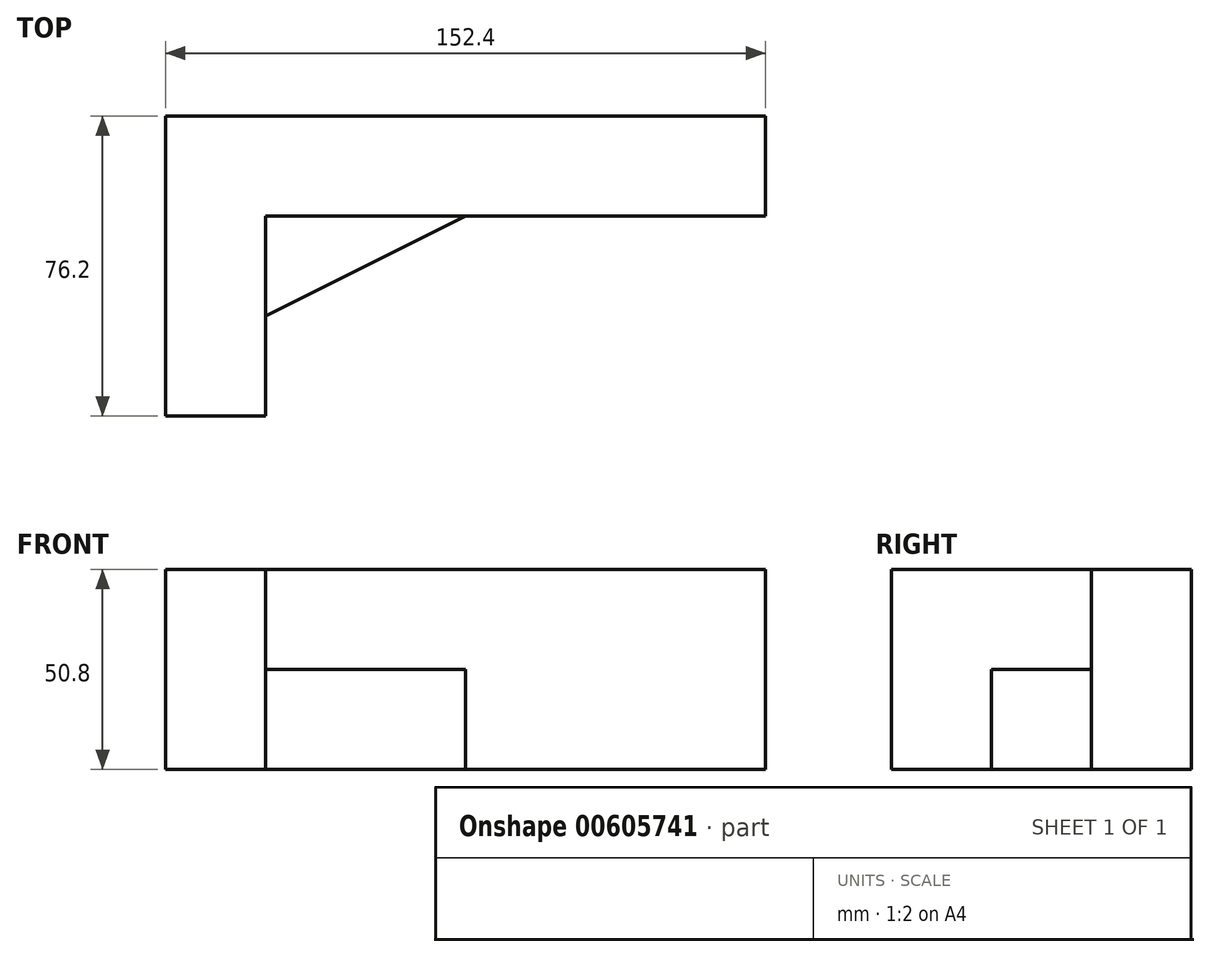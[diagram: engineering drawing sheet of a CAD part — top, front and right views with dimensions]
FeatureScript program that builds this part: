
annotation { "Feature Type Name" : "Feature", "Feature Type Description" : "" }
export const myFeature = defineFeature(function(context is Context, id is Id, definition is map)
    precondition{}
    {
        {
            var Q0;
            Q0=qCreatedBy(makeId("Front.planeOp"),FACE);
            var sketch = newSketch(context, id + "F0", { "sketchPlane" : qUnion([Q0])});
            skLineSegment(sketch, "E0", {"start": v(0, 0) * mm, "end": v(152.4, 0) * mm});
            skLineSegment(sketch, "E1", {"start": v(152.4, 0) * mm, "end": v(152.4, 50.8) * mm});
            skLineSegment(sketch, "E2", {"start": v(152.4, 50.8) * mm, "end": v(0, 50.8) * mm});
            skLineSegment(sketch, "E3", {"start": v(0, 50.8) * mm, "end": v(0, 0) * mm});
            skLineSegment(sketch, "E4.0", {"start": v(25.4, 50.8) * mm, "end": v(25.4, 0) * mm});
            skLineSegment(sketch, "E5", {"start": v(25.4, 25.4) * mm, "end": v(76.2, 25.4) * mm});
            skLineSegment(sketch, "E6", {"start": v(76.2, 25.4) * mm, "end": v(76.2, 0) * mm});
            skSolve(sketch);
        }
        {
            var Q0;
            {var subQ4=sQuery(id+"F0.wireOp",EDGE,"E3");Q0=makeQuery(id+"F0.imprint","IMPRINT",FACE,{"disambiguationData":[TD([[makeQuery(id+"F0.imprint","IMPRINT",EDGE,{"derivedFrom":subQ4}),1.0]])]});}
            extrude(context, id + "F1", {"entities" : qUnion([Q0]), "depth" : 76.2 * mm, "offsetDistance" : 25.4 * mm});
        }
        {
            var Q0;
            {var subQ1=sQuery(id+"F0.wireOp",EDGE,"E1");Q0=makeQuery(id+"F0.imprint","IMPRINT",FACE,{"disambiguationData":[TD([[makeQuery(id+"F0.imprint","IMPRINT",EDGE,{"derivedFrom":subQ1}),1.0]])]});}
            extrude(context, id + "F2", {"entities" : qUnion([Q0]), "operationType" : NewBodyOperationType.ADD, "depth" : 25.4 * mm, "offsetDistance" : 25.4 * mm});
        }
        {
            var Q0;
            {var subQ4=sQuery(id+"F0.wireOp",EDGE,"E5");Q0=makeQuery(id+"F0.imprint","IMPRINT",FACE,{"disambiguationData":[TD([[makeQuery(id+"F0.imprint","IMPRINT",EDGE,{"derivedFrom":subQ4}),-1.0]])]});}
            extrude(context, id + "F3", {"entities" : qUnion([Q0]), "operationType" : NewBodyOperationType.ADD, "depth" : 50.8 * mm, "offsetDistance" : 25.4 * mm});
        }
        {
            var Q0;
            Q0=makeQuery(id+"F3.opExtrude","SWEPT_FACE",FACE,{"disambiguationData":[OSD([sQuery(id+"F0.wireOp",EDGE,"E5")])]});
            var sketch = newSketch(context, id + "F4", { "sketchPlane" : qUnion([Q0])});
            skLineSegment(sketch, "E7", {"start": v(25.4, -50.8) * mm, "end": v(76.2, -25.4) * mm});
            skSolve(sketch);
        }
        {
            var Q0;
            Q0=makeQuery(id+"F4.imprint","IMPRINT",FACE,{"disambiguationData":[TD([[makeQuery(id+"F4.imprint","IMPRINT",EDGE,{"derivedFrom":sQuery(id+"F4.wireOp",EDGE,"E7")}),-1.0]])]});
            extrude(context, id + "F5", {"entities" : qUnion([Q0]), "operationType" : NewBodyOperationType.REMOVE, "oppositeDirection" : true, "depth" : 25.4 * mm, "offsetDistance" : 25.4 * mm});
        }
    });
